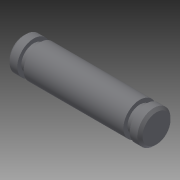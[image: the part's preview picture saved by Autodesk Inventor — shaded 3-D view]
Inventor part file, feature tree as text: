
AUTODESK INVENTOR PART (.ipt)
format: ipt  version: 2014 (Build 180170000, 170)  size: 122,368 bytes
history: native  units: in
note: dims shown in document units (in); Inventor stores cm internally (conversion verified against a paired STEP export)
features: other x21, revolve x1, sketch x1
ambient origin geometry x8: Origin, YZ Plane, XZ Plane, XY Plane, X Axis, Y Axis, Z Axis, Center Point
bodies: Solid1 (feature_tree)
feature tree (23):
  revolve  "Revolution1"  [1 undecoded]
  other  "pin_XY"
  other  "pin_YZ"
  other  "pin_ZX"
  other  "pin_X"
  other  "pin_Y"
  other  "pin_Z"
  other  "pin_Center"
  other  "rr1_XY"
  other  "rr1_YZ"
  other  "rr1_ZX"
  other  "rr1_X"
  other  "rr1_Y"
  other  "rr1_Z"
  other  "rr1_Center"
  other  "rr2_XY"
  other  "rr2_YZ"
  other  "rr2_ZX"
  other  "rr2_X"
  other  "rr2_Y"
  other  "rr2_Z"
  other  "rr2_Center"
  sketch  "Sketch_1"  dims[d0=360.0deg]
note: 1 required parameter value undecoded (feature->parameter linkage not recoverable at this tier; creation-order binding heuristic only, values carry confidence <= 0.55)
